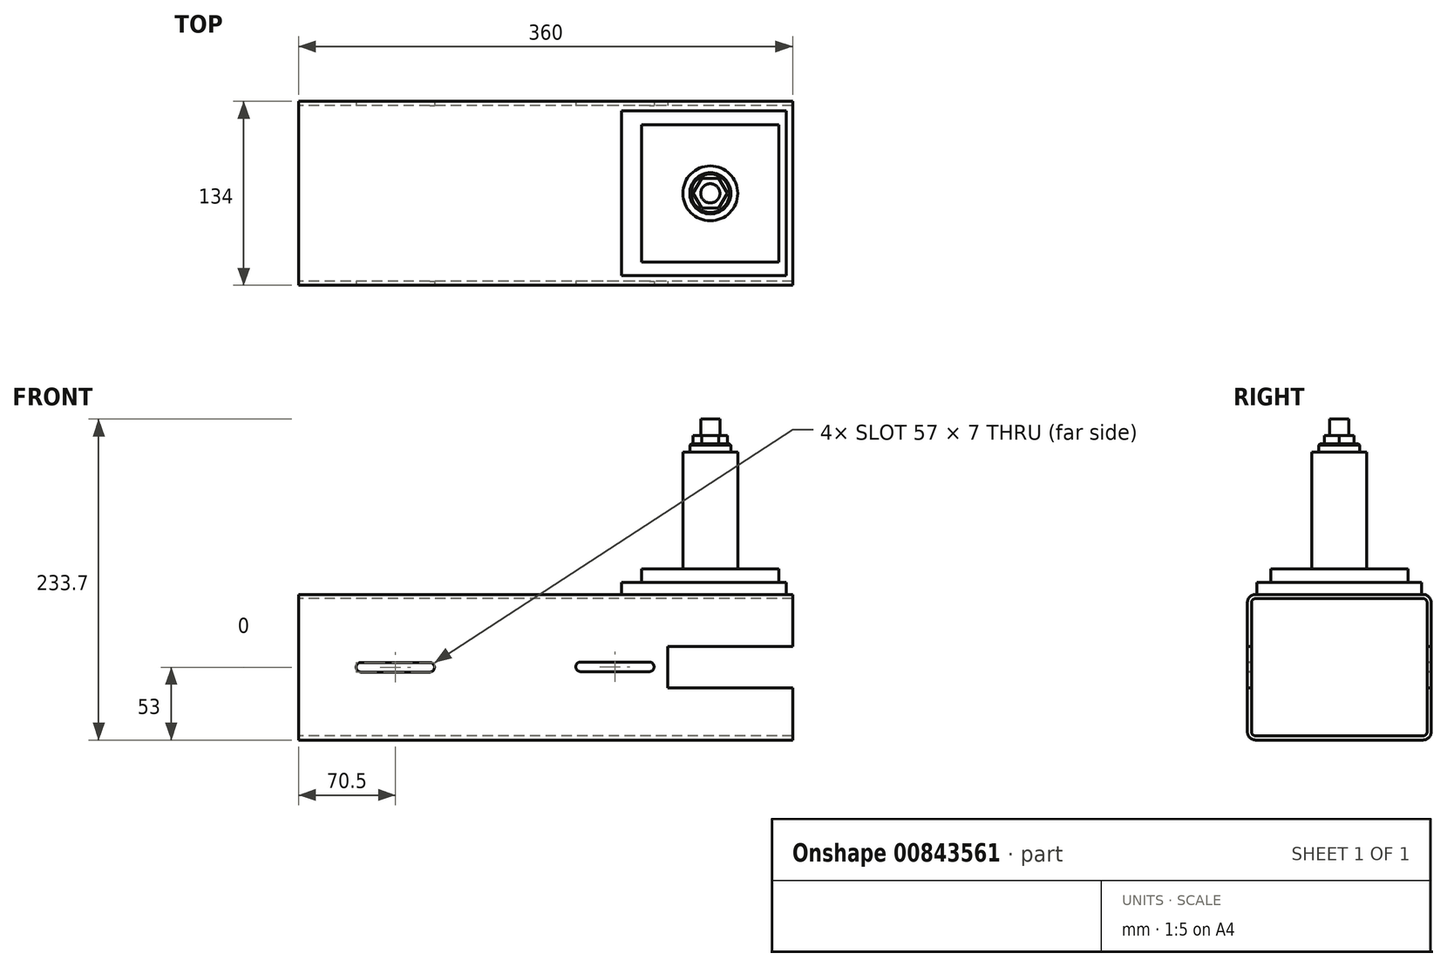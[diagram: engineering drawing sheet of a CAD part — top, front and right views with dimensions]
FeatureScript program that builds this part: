
annotation { "Feature Type Name" : "Feature", "Feature Type Description" : "" }
export const myFeature = defineFeature(function(context is Context, id is Id, definition is map)
    precondition{}
    {
        {
            var Q0;
            Q0=qCreatedBy(makeId("Top.planeOp"),FACE);
            var sketch = newSketch(context, id + "F0", { "sketchPlane" : qUnion([Q0])});
            skCircle(sketch, "E0", {"center": v(0, 0) * mm, "radius": 20 * mm});
            skSolve(sketch);
        }
        {
            var Q0;
            Q0 = qSketchRegion(id + "F0", true);
            extrude(context, id + "F1", {"entities" : qUnion([Q0]), "depth" : 85 * mm, "offsetDistance" : 25 * mm});
        }
        {
            var Q0;
            Q0=qCreatedBy(makeId("Top.planeOp"),FACE);
            var sketch = newSketch(context, id + "F2", { "sketchPlane" : qUnion([Q0])});
            skLineSegment(sketch, "E1.bottom", {"start": v(-50, -50) * mm, "end": v(50, -50) * mm});
            skLineSegment(sketch, "E1.top", {"start": v(-50, 50) * mm, "end": v(50, 50) * mm});
            skLineSegment(sketch, "E1.left", {"start": v(-50, -50) * mm, "end": v(-50, 50) * mm});
            skLineSegment(sketch, "E1.right", {"start": v(50, -50) * mm, "end": v(50, 50) * mm});
            skPoint(sketch, "E1.middle", {"position": v(0, 0) * mm});
            skSolve(sketch);
        }
        {
            var Q0;
            Q0 = qSketchRegion(id + "F2", true);
            extrude(context, id + "F3", {"entities" : qUnion([Q0]), "operationType" : NewBodyOperationType.ADD, "oppositeDirection" : true, "depth" : 10 * mm, "offsetDistance" : 25 * mm});
        }
        {
            var Q0;
            Q0=makeQuery(id+"F3.opExtrude","CAP_FACE",FACE,{"disambiguationData":[OSD([sQuery(id+"F2.wireOp",EDGE,"E1.bottom"),sQuery(id+"F2.wireOp",EDGE,"E1.top"),sQuery(id+"F2.wireOp",EDGE,"E1.left"),sQuery(id+"F2.wireOp",EDGE,"E1.right")])],"isStart":false});
            var sketch = newSketch(context, id + "F4", { "sketchPlane" : qUnion([Q0])});
            skLineSegment(sketch, "E2.bottom", {"start": v(55.34, -60) * mm, "end": v(-64.66, -60) * mm});
            skLineSegment(sketch, "E2.top", {"start": v(55.34, 60) * mm, "end": v(-64.66, 60) * mm});
            skLineSegment(sketch, "E2.left", {"start": v(55.34, -60) * mm, "end": v(55.34, 60) * mm});
            skLineSegment(sketch, "E2.right", {"start": v(-64.66, -60) * mm, "end": v(-64.66, 60) * mm});
            skPoint(sketch, "E2.middle", {"position": v(-4.66, 0) * mm});
            skSolve(sketch);
        }
        {
            var Q0;
            Q0 = qSketchRegion(id + "F4", true);
            extrude(context, id + "F5", {"entities" : qUnion([Q0]), "operationType" : NewBodyOperationType.ADD, "depth" : 10 * mm, "offsetDistance" : 25 * mm});
        }
        {
            var Q0;
            Q0=makeQuery(id+"F1.opExtrude","CAP_FACE",FACE,{"disambiguationData":[OSD([sQuery(id+"F0.wireOp",EDGE,"E0")])],"isStart":false});
            var sketch = newSketch(context, id + "F6", { "sketchPlane" : qUnion([Q0])});
            skCircle(sketch, "E3", {"center": v(0, 0) * mm, "radius": 15 * mm});
            skSolve(sketch);
        }
        {
            var Q0;
            Q0 = qSketchRegion(id + "F6", true);
            extrude(context, id + "F7", {"entities" : qUnion([Q0]), "operationType" : NewBodyOperationType.ADD, "depth" : 6 * mm, "offsetDistance" : 25 * mm});
        }
        {
            var Q0;
            Q0=makeQuery(id+"F7.opExtrude","CAP_EDGE",EDGE,{"disambiguationData":[OSD([sQuery(id+"F6.wireOp",EDGE,"E3")])],"isStart":false});
            chamfer(context, id + "F8", {"entities" : qUnion([Q0]), "width" : 1 * mm, "tangentPropagation" : true});
        }
        {
            var Q0;
            Q0=makeQuery(id+"F7.opExtrude","CAP_FACE",FACE,{"disambiguationData":[OSD([sQuery(id+"F6.wireOp",EDGE,"E3")])],"isStart":false});
            var sketch = newSketch(context, id + "F9", { "sketchPlane" : qUnion([Q0])});
            skCircle(sketch, "E4.cCircle", {"center": v(0, 0) * mm, "radius": 12.5 * mm, "construction": true});
            skLineSegment(sketch, "E4.0", {"start": v(-12.5, 0) * mm, "end": v(-6.25, 10.83) * mm});
            skLineSegment(sketch, "E4.1", {"start": v(-6.25, 10.83) * mm, "end": v(6.25, 10.83) * mm});
            skLineSegment(sketch, "E4.2", {"start": v(6.25, 10.83) * mm, "end": v(12.5, 0) * mm});
            skLineSegment(sketch, "E4.3", {"start": v(12.5, 0) * mm, "end": v(6.25, -10.83) * mm});
            skLineSegment(sketch, "E4.4", {"start": v(6.25, -10.83) * mm, "end": v(-6.25, -10.83) * mm});
            skLineSegment(sketch, "E4.5", {"start": v(-6.25, -10.83) * mm, "end": v(-12.5, 0) * mm});
            skSolve(sketch);
        }
        {
            var Q0;
            Q0 = qSketchRegion(id + "F9", true);
            extrude(context, id + "F10", {"entities" : qUnion([Q0]), "operationType" : NewBodyOperationType.ADD, "depth" : 6 * mm, "offsetDistance" : 25 * mm});
        }
        {
            var Q0;
            Q0=makeQuery(id+"F10.opExtrude","CAP_FACE",FACE,{"disambiguationData":[OSD([sQuery(id+"F9.wireOp",EDGE,"E4.0"),sQuery(id+"F9.wireOp",EDGE,"E4.1"),sQuery(id+"F9.wireOp",EDGE,"E4.2"),sQuery(id+"F9.wireOp",EDGE,"E4.3"),sQuery(id+"F9.wireOp",EDGE,"E4.4"),sQuery(id+"F9.wireOp",EDGE,"E4.5")])],"isStart":false});
            var sketch = newSketch(context, id + "F11", { "sketchPlane" : qUnion([Q0])});
            skCircle(sketch, "E5", {"center": v(0, 0) * mm, "radius": 7 * mm});
            skSolve(sketch);
        }
        {
            var Q0;
            Q0 = qSketchRegion(id + "F11", true);
            extrude(context, id + "F12", {"entities" : qUnion([Q0]), "operationType" : NewBodyOperationType.ADD, "depth" : 12 * mm, "offsetDistance" : 25 * mm});
        }
        {
            var Q0;
            Q0=qCreatedBy(makeId("Right.planeOp"),FACE);
            var sketch = newSketch(context, id + "F13", { "sketchPlane" : qUnion([Q0])});
            skLineSegment(sketch, "E6.bottom", {"start": v(-61, -18.7) * mm, "end": v(61, -18.7) * mm});
            skLineSegment(sketch, "E6.top", {"start": v(-61, -124.7) * mm, "end": v(61, -124.7) * mm});
            skLineSegment(sketch, "E6.left", {"start": v(-67, -24.7) * mm, "end": v(-67, -118.7) * mm});
            skLineSegment(sketch, "E6.right", {"start": v(67, -24.7) * mm, "end": v(67, -118.7) * mm});
            skPoint(sketch, "E7", {"position": v(0, -18.7) * mm});
            skPoint(sketch, "E8.visualSharp", {"position": v(-67, -18.7) * mm});
            skArc(sketch, "E8.filletArc", {"start": v(-61, -18.7) * mm, "mid": v(-65.24, -20.46) * mm, "end": v(-67, -24.7) * mm});
            skPoint(sketch, "E9.visualSharp", {"position": v(67, -18.7) * mm});
            skArc(sketch, "E9.filletArc", {"start": v(67, -24.7) * mm, "mid": v(65.24, -20.46) * mm, "end": v(61, -18.7) * mm});
            skPoint(sketch, "E10.visualSharp", {"position": v(-67, -124.7) * mm});
            skArc(sketch, "E10.filletArc", {"start": v(-67, -118.7) * mm, "mid": v(-65.24, -122.94) * mm, "end": v(-61, -124.7) * mm});
            skPoint(sketch, "E11.visualSharp", {"position": v(67, -124.7) * mm});
            skArc(sketch, "E11.filletArc", {"start": v(61, -124.7) * mm, "mid": v(65.24, -122.94) * mm, "end": v(67, -118.7) * mm});
            skLineSegment(sketch, "E12.0", {"start": v(-64, -24.7) * mm, "end": v(-64, -118.7) * mm});
            skArc(sketch, "E13.0", {"start": v(-61, -21.7) * mm, "mid": v(-63.12, -22.58) * mm, "end": v(-64, -24.7) * mm});
            skLineSegment(sketch, "E14.0", {"start": v(-61, -21.7) * mm, "end": v(61, -21.7) * mm});
            skArc(sketch, "E15.0", {"start": v(64, -24.7) * mm, "mid": v(63.12, -22.58) * mm, "end": v(61, -21.7) * mm});
            skLineSegment(sketch, "E16.0", {"start": v(64, -24.7) * mm, "end": v(64, -118.7) * mm});
            skArc(sketch, "E17.0", {"start": v(61, -121.7) * mm, "mid": v(63.12, -120.82) * mm, "end": v(64, -118.7) * mm});
            skArc(sketch, "E18.0", {"start": v(-64, -118.7) * mm, "mid": v(-63.12, -120.82) * mm, "end": v(-61, -121.7) * mm});
            skLineSegment(sketch, "E18.2", {"start": v(-61, -121.7) * mm, "end": v(61, -121.7) * mm});
            skSolve(sketch);
        }
        {
            var Q0;
            Q0 = qSketchRegion(id + "F13", true);
            extrude(context, id + "F14", {"entities" : qUnion([Q0]), "operationType" : NewBodyOperationType.ADD, "depth" : 60 * mm, "offsetDistance" : 25 * mm, "hasSecondDirection" : true, "secondDirectionOppositeDirection" : true, "secondDirectionDepth" : 300 * mm});
        }
        {
            var Q0;
            Q0=makeQuery(id+"F14.opExtrude","SWEPT_FACE",FACE,{"disambiguationData":[OSD([sQuery(id+"F13.wireOp",EDGE,"E6.left")])]});
            var sketch = newSketch(context, id + "F15", { "sketchPlane" : qUnion([Q0])});
            skArc(sketch, "E19.0.startCap", {"start": v(-254.5, -75.2) * mm, "mid": v(-258, -71.7) * mm, "end": v(-254.5, -68.2) * mm});
            skArc(sketch, "E19.0.endCap", {"start": v(-204.5, -68.2) * mm, "mid": v(-201, -71.7) * mm, "end": v(-204.5, -75.2) * mm});
            skLineSegment(sketch, "E19.0.left", {"start": v(-254.5, -68.2) * mm, "end": v(-204.5, -68.2) * mm});
            skLineSegment(sketch, "E19.0.right", {"start": v(-254.5, -75.2) * mm, "end": v(-204.5, -75.2) * mm});
            skLineSegment(sketch, "E20.1.0.0", {"start": v(-94.5, -67.91) * mm, "end": v(-44.5, -67.91) * mm});
            skLineSegment(sketch, "E20.1.0.1", {"start": v(-94.5, -74.91) * mm, "end": v(-44.5, -74.91) * mm});
            skArc(sketch, "E20.1.0.2", {"start": v(-44.5, -67.91) * mm, "mid": v(-41, -71.41) * mm, "end": v(-44.5, -74.91) * mm});
            skArc(sketch, "E20.1.0.3", {"start": v(-94.5, -74.91) * mm, "mid": v(-98, -71.41) * mm, "end": v(-94.5, -67.91) * mm});
            skLineSegment(sketch, "E20.direction1", {"start": v(-254.5, -75.2) * mm, "end": v(-94.5, -74.91) * mm, "construction": true});
            skSolve(sketch);
        }
        {
            var Q0;
            Q0 = qSketchRegion(id + "F15", true);
            extrude(context, id + "F16", {"entities" : qUnion([Q0]), "operationType" : NewBodyOperationType.REMOVE, "endBound" : BoundingType.THROUGH_ALL, "oppositeDirection" : true, "depth" : 25 * mm, "offsetDistance" : 25 * mm});
        }
        {
            var Q0;
            Q0=makeQuery(id+"F14.opExtrude","SWEPT_FACE",FACE,{"disambiguationData":[OSD([sQuery(id+"F13.wireOp",EDGE,"E6.left")])]});
            var sketch = newSketch(context, id + "F17", { "sketchPlane" : qUnion([Q0])});
            skLineSegment(sketch, "E21.bottom", {"start": v(-31, -56.7) * mm, "end": v(151, -56.7) * mm});
            skLineSegment(sketch, "E21.top", {"start": v(-31, -86.7) * mm, "end": v(151, -86.7) * mm});
            skLineSegment(sketch, "E21.left", {"start": v(-31, -56.7) * mm, "end": v(-31, -86.7) * mm});
            skLineSegment(sketch, "E21.right", {"start": v(151, -56.7) * mm, "end": v(151, -86.7) * mm});
            skPoint(sketch, "E21.middle", {"position": v(60, -71.7) * mm});
            skSolve(sketch);
        }
        {
            var Q0;
            Q0 = qSketchRegion(id + "F17", true);
            extrude(context, id + "F18", {"entities" : qUnion([Q0]), "operationType" : NewBodyOperationType.REMOVE, "endBound" : BoundingType.THROUGH_ALL, "oppositeDirection" : true, "depth" : 25 * mm, "offsetDistance" : 25 * mm});
        }
    });
